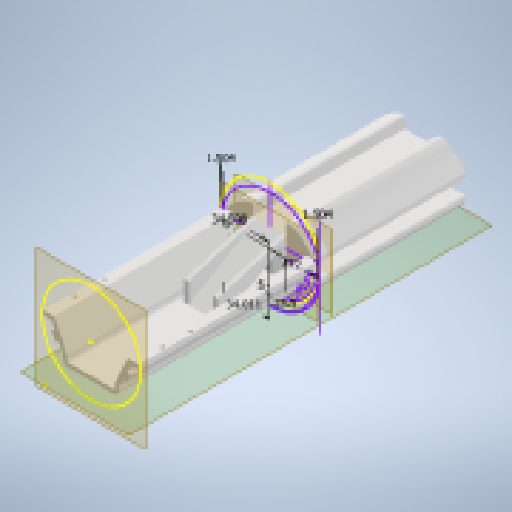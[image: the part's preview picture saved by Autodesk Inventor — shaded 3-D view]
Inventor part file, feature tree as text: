
AUTODESK INVENTOR PART (.ipt)
format: ipt  version: 2023 (Build 270158030, 158C)  size: 495,616 bytes
history: native  units: in
note: dims shown in document units (in); Inventor stores cm internally (conversion verified against a paired STEP export)
features: sketch x15, extrude x9, plane x6, chamfer x4, reference x3, other x3, projected_geometry x2, fillet x1
ambient origin geometry x8: Origin, YZ Plane, XZ Plane, XY Plane, X Axis, Y Axis, Z Axis, Center Point
bodies: Body1 (feature_tree)
feature tree (43):
  sketch  "Sketch1"  dims[d22=3.937in d23=0.0in d24=0.0in]
  sketch  "Sketch7"  dims[d25=0.3937in d26=0.0in d27=0.1969in d28=1.122in]
  extrude  "Extrusion3"  TaperAngle=0.0deg  [1 undecoded]
  plane  "Work Plane3"
  extrude  "Extrusion4"  Depth=0.1969in
  sketch  "Sketch11"  dims[d39=1.339in d42=0.1969in d43=1.122in]
  sketch  "Sketch12"  dims[d44=0.0in d45=0.0in]
  plane  "Work Plane4"
  extrude  "Extrusion5"  Depth=0.0592in
  sketch  "Sketch14"  dims[d62=0.1181in]
  plane  "Work Plane5"
  sketch  "Sketch15"  dims[d96=0.0394in]
  fillet  "Fillet2"  Radius=0.0592in
  plane  "Work Plane6"
  extrude  "Extrusion11"  TaperAngle=0.0deg  [1 undecoded]
  plane  "Work Plane7"
  extrude  "Extrusion12"  Depth=0.1969in
  plane  "Work Plane8"
  sketch  "Sketch19"  dims[d99=0.2362in]
  sketch  "Sketch20"  dims[d100=0.7874in]
  extrude  "Extrusion13"  TaperAngle=0.0deg  [1 undecoded]
  extrude  "Extrusion15"  Depth=5.1181in TaperAngle=0.0deg
  chamfer  "Chamfer11"  [1 undecoded]
  extrude  "Extrusion16"  Depth=0.1969in
  chamfer  "Chamfer12"  Distance=0.315in
  extrude  "Extrusion17"  Depth=0.1969in
  chamfer  "Chamfer13"  Distance=0.1181in
  chamfer  "Chamfer14"  Distance=0.1181in
  reference  "Reference1"
  sketch  "Sketch8"  dims[d31=2.8346in d35=0.0592in d36=0.0592in]
  sketch  "Sketch10"  dims[d37=1.3586in d38=0.0in]
  projected_geometry  "Projected Loop1"
  reference  "Reference2"
  sketch  "Sketch13"  dims[d46=0.1969in d47=1.122in d48=0.0in d53=5.1181in d54=0.0in]
  projected_geometry  "Projected Loop3"
  sketch  "Sketch17"  dims[d97=0.0in]
  sketch  "Sketch18"  dims[d98=0.2362in]
  reference  "Reference3"
  sketch  "Sketch21"  dims[d101=0.7874in d102=0.0in d103=0.0in]
  sketch  "Sketch23"  dims[d104=0.315in d105=0.7874in d106=0.315in d107=0.7874in d108=0.1181in d109=0.0in d110=0.1181in d111=0.1181in d112=0.1181in d113=0.1181in d114=0.7874in d115=1.5748in d116=0.7874in d117=1.5748in d118=0.0in d119=0.0in d120=1.9685in d121=1.9685in d123=0.0984in d124=0.0984in d125=0.0984in d126=0.0984in d139=1.1654in d140=0.0in d141=1.9685in d142=1.1654in d143=45.0deg d144=1.1654in d145=0.0in d146=1.9685in d147=0.5827in d148=45.0deg d149=0.1969in d150=1.1654in d151=0.0in d152=0.0787in d153=0.1969in d154=45.0deg d155=0.0787in d156=0.1969in d157=45.0deg d49=0.0197in d50=0.0344in d51=0.0197in d52=0.0344in d55=0.0197in d56=0.0344in d87=0.0197in d88=0.0344in d89=0.0197in d90=0.0344in]
  other  "<userpath>\OneDrive - med.cornell.edu\Desktop\3D Print Designs\62mmHolder_V3\Assembly1.iam"
  other  "Assembly1.iam"
  other  "62mmAdapter:1"
note: 4 required parameter values undecoded (feature->parameter linkage not recoverable at this tier; creation-order binding heuristic only, values carry confidence <= 0.55)
